FCSTD DOCUMENT  (FreeCAD 0.19R)
Label: quadcopter
License: All rights reserved
LicenseURL: http://en.wikipedia.org/wiki/All_rights_reserved
objects: Sketcher::SketchObject×3, PartDesign::Body×1
note: 4 computed .brp shape members not serialized (recipe doc carries the construction recipe); baked Part::Feature solids carry a one-line shape summary decoded from their .brp

FEATURE [Sketcher::SketchObject] Sketch001
  FullyConstrained = true
  sketch-geometry (20):
    g0: Circle CenterX=50 CenterY=-50 CenterZ=0 NormalX=0 NormalY=0 NormalZ=1 AngleXU=0 Radius=14
    g1: Circle CenterX=50 CenterY=-58 CenterZ=0 NormalX=0 NormalY=0 NormalZ=1 AngleXU=0 Radius=1.5
    g2: Circle CenterX=50 CenterY=-42 CenterZ=0 NormalX=0 NormalY=0 NormalZ=1 AngleXU=0 Radius=1.5
    g3: Circle CenterX=59.5 CenterY=-50 CenterZ=0 NormalX=0 NormalY=0 NormalZ=1 AngleXU=0 Radius=1.5
    g4: Circle CenterX=40.5 CenterY=-50 CenterZ=0 NormalX=0 NormalY=0 NormalZ=1 AngleXU=0 Radius=1.5
    g5: Circle CenterX=50 CenterY=50 CenterZ=0 NormalX=0 NormalY=0 NormalZ=1 AngleXU=0 Radius=14
    g6: Circle CenterX=50 CenterY=58 CenterZ=0 NormalX=0 NormalY=0 NormalZ=1 AngleXU=0 Radius=1.5
    g7: Circle CenterX=50 CenterY=42 CenterZ=0 NormalX=0 NormalY=0 NormalZ=1 AngleXU=0 Radius=1.5
    g8: Circle CenterX=59.5 CenterY=50 CenterZ=0 NormalX=0 NormalY=0 NormalZ=1 AngleXU=0 Radius=1.5
    g9: Circle CenterX=40.5 CenterY=50 CenterZ=0 NormalX=0 NormalY=0 NormalZ=1 AngleXU=0 Radius=1.5
    g10: Circle CenterX=-50 CenterY=-50 CenterZ=0 NormalX=0 NormalY=0 NormalZ=1 AngleXU=0 Radius=14
    g11: Circle CenterX=-50 CenterY=-58 CenterZ=0 NormalX=0 NormalY=0 NormalZ=1 AngleXU=0 Radius=1.5
    g12: Circle CenterX=-50 CenterY=-42 CenterZ=0 NormalX=0 NormalY=0 NormalZ=1 AngleXU=0 Radius=1.5
    g13: Circle CenterX=-59.5 CenterY=-50 CenterZ=0 NormalX=0 NormalY=0 NormalZ=1 AngleXU=0 Radius=1.5
    g14: Circle CenterX=-40.5 CenterY=-50 CenterZ=0 NormalX=0 NormalY=0 NormalZ=1 AngleXU=0 Radius=1.5
    g15: Circle CenterX=-50 CenterY=50 CenterZ=0 NormalX=0 NormalY=0 NormalZ=1 AngleXU=0 Radius=14
    g16: Circle CenterX=-50 CenterY=58 CenterZ=0 NormalX=0 NormalY=0 NormalZ=1 AngleXU=0 Radius=1.5
    g17: Circle CenterX=-50 CenterY=42 CenterZ=0 NormalX=0 NormalY=0 NormalZ=1 AngleXU=0 Radius=1.5
    g18: Circle CenterX=-59.5 CenterY=50 CenterZ=0 NormalX=0 NormalY=0 NormalZ=1 AngleXU=0 Radius=1.5
    g19: Circle CenterX=-40.5 CenterY=50 CenterZ=0 NormalX=0 NormalY=0 NormalZ=1 AngleXU=0 Radius=1.5
  constraints (49):
    c: Symmetric(g3,g4,g0)
    c: Symmetric(g1,g2,g0)
    c: Diameter(g0) = 28
    c: Diameter(g4) = 3
    c: Equal(g4,g1)
    c: Equal(g1,g3)
    c: Equal(g3,g2)
    c: Symmetric(g8,g9,g5)
    c: Symmetric(g6,g7,g5)
    c: Diameter(g5) = 28
    c: Diameter(g9) = 3
    c: Equal(g9,g6)
    c: Equal(g6,g8)
    c: Equal(g8,g7)
    c: Symmetric(g13,g14,g10)
    c: Symmetric(g11,g12,g10)
    c: Diameter(g10) = 28
    c: Diameter(g14) = 3
    c: Equal(g14,g11)
    c: Equal(g11,g13)
    c: Equal(g13,g12)
    c: Symmetric(g18,g19,g15)
    c: Symmetric(g16,g17,g15)
    c: DistanceX(g18,g19) = 19
    c: DistanceY(g17,g16) = 16
    c: Diameter(g15) = 28
    c: DistanceX(g15,g-1) = 50
    c: DistanceY(g-1,g15) = 50
    c: Diameter(g19) = 3
    c: Equal(g19,g16)
    c: Equal(g16,g18)
    c: Equal(g18,g17)
    c: Vertical(g16,g17)
    c: Horizontal(g18,g19)
    c: Symmetric(g10,g15,g-1)
    c: Symmetric(g0,g15,g-1)
    c: Symmetric(g5,g10,g-1)
    c: DistanceX(g13,g14) = 19
    c: DistanceY(g11,g12) = 16
    c: Horizontal(g10,g14)
    c: Vertical(g12,g10)
    c: DistanceY(g1,g2) = 16
    c: DistanceX(g4,g3) = 19
    c: Horizontal(g4,g0)
    c: Vertical(g2,g0)
    c: DistanceY(g7,g6) = 16
    c: DistanceX(g9,g8) = 19
    c: Vertical(g5,g6)
    c: Horizontal(g9,g5)
FEATURE [Sketcher::SketchObject] Sketch
  FullyConstrained = true
  MapMode = 5
  Support = -> [XY_Plane]
  sketch-geometry (4):
    g0: LineSegment StartX=-17.5 StartY=53 StartZ=0 EndX=17.5 EndY=53 EndZ=0
    g1: LineSegment StartX=17.5 StartY=53 StartZ=0 EndX=17.5 EndY=-53 EndZ=0
    g2: LineSegment StartX=17.5 StartY=-53 StartZ=0 EndX=-17.5 EndY=-53 EndZ=0
    g3: LineSegment StartX=-17.5 StartY=-53 StartZ=0 EndX=-17.5 EndY=53 EndZ=0
  constraints (11):
    c: Coincident(g0,g1)
    c: Coincident(g1,g2)
    c: Coincident(g2,g3)
    c: Coincident(g3,g0)
    c: Horizontal(g0)
    c: Horizontal(g2)
    c: Vertical(g1)
    c: Vertical(g3)
    c: DistanceY(g1,g1) = 106
    c: DistanceX(g0,g0) = 35
    c: Symmetric(g0,g1,g-1)
FEATURE [Sketcher::SketchObject] Sketch004
  FullyConstrained = true
  sketch-geometry (24):
    g0: LineSegment StartX=-7.24e-14 StartY=-3.6e-14 StartZ=0 EndX=-98.9949 EndY=-98.9949 EndZ=0
    g1: ArcOfCircle CenterX=-7.24e-14 CenterY=-3.6e-14 CenterZ=0 NormalX=0 NormalY=0 NormalZ=1 AngleXU=0 Radius=17.5 StartAngle=5.49779 EndAngle=8.63938
    g2: ArcOfCircle CenterX=-98.9949 CenterY=-98.9949 CenterZ=0 NormalX=0 NormalY=0 NormalZ=1 AngleXU=0 Radius=17.5 StartAngle=2.35619 EndAngle=5.49779
    g3: LineSegment StartX=-12.3744 StartY=12.3744 StartZ=0 EndX=-111.369 EndY=-86.6206 EndZ=0
    g4: LineSegment StartX=-86.6206 StartY=-111.369 StartZ=0 EndX=12.3744 EndY=-12.3744 EndZ=0
    g5: LineSegment StartX=-86.6206 StartY=-111.369 StartZ=0 EndX=-111.369 EndY=-86.6206 EndZ=0
    g6: LineSegment StartX=-7.24e-14 StartY=-3.6e-14 StartZ=0 EndX=98.9949 EndY=-98.9949 EndZ=0
    g7: ArcOfCircle CenterX=-7.24e-14 CenterY=-3.6e-14 CenterZ=0 NormalX=0 NormalY=0 NormalZ=1 AngleXU=0 Radius=17.5 StartAngle=0.785398 EndAngle=3.92699
    g8: ArcOfCircle CenterX=98.9949 CenterY=-98.9949 CenterZ=0 NormalX=0 NormalY=0 NormalZ=1 AngleXU=0 Radius=17.5 StartAngle=3.92699 EndAngle=7.06858
    g9: LineSegment StartX=12.3744 StartY=12.3744 StartZ=0 EndX=111.369 EndY=-86.6206 EndZ=0
    g10: LineSegment StartX=86.6206 StartY=-111.369 StartZ=0 EndX=-12.3744 EndY=-12.3744 EndZ=0
    g11: LineSegment StartX=86.6206 StartY=-111.369 StartZ=0 EndX=111.369 EndY=-86.6206 EndZ=0
    g12: LineSegment StartX=-7.24e-14 StartY=-3.6e-14 StartZ=0 EndX=-98.9949 EndY=98.9949 EndZ=0
    g13: ArcOfCircle CenterX=-7.24e-14 CenterY=-3.6e-14 CenterZ=0 NormalX=0 NormalY=0 NormalZ=1 AngleXU=0 Radius=17.5 StartAngle=3.92699 EndAngle=7.06858
    g14: ArcOfCircle CenterX=-98.9949 CenterY=98.9949 CenterZ=0 NormalX=0 NormalY=0 NormalZ=1 AngleXU=0 Radius=17.5 StartAngle=0.785398 EndAngle=3.92699
    g15: LineSegment StartX=-12.3744 StartY=-12.3744 StartZ=0 EndX=-111.369 EndY=86.6206 EndZ=0
    g16: LineSegment StartX=-86.6206 StartY=111.369 StartZ=0 EndX=12.3744 EndY=12.3744 EndZ=0
    g17: LineSegment StartX=-86.6206 StartY=111.369 StartZ=0 EndX=-111.369 EndY=86.6206 EndZ=0
    g18: LineSegment StartX=0 StartY=0 StartZ=0 EndX=98.9949 EndY=98.9949 EndZ=0
    g19: ArcOfCircle CenterX=0 CenterY=0 CenterZ=0 NormalX=0 NormalY=0 NormalZ=1 AngleXU=0 Radius=17.5 StartAngle=2.35619 EndAngle=5.49779
    g20: ArcOfCircle CenterX=98.9949 CenterY=98.9949 CenterZ=0 NormalX=0 NormalY=0 NormalZ=1 AngleXU=0 Radius=17.5 StartAngle=5.49779 EndAngle=8.63938
    g21: LineSegment StartX=12.3744 StartY=-12.3744 StartZ=0 EndX=111.369 EndY=86.6206 EndZ=0
    g22: LineSegment StartX=86.6206 StartY=111.369 StartZ=0 EndX=-12.3744 EndY=12.3744 EndZ=0
    g23: LineSegment StartX=86.6206 StartY=111.369 StartZ=0 EndX=111.369 EndY=86.6206 EndZ=0
  constraints (53):
    c: Distance(g0) = 140
    c: Tangent(g1,g3) = -1.5708
    c: Tangent(g3,g2) = -1.5708
    c: Tangent(g2,g4) = -1.5708
    c: Tangent(g4,g1) = -1.5708
    c: Equal(g1,g2)
    c: Coincident(g1,g0)
    c: Coincident(g2,g0)
    c: Coincident(g5,g2)
    c: Coincident(g5,g2)
    c: Distance(g5) = 35
    c: Distance(g6) = 140
    c: Tangent(g7,g9) = 1.5708
    c: Tangent(g9,g8) = 1.5708
    c: Tangent(g8,g10) = 1.5708
    c: Tangent(g10,g7) = 1.5708
    c: Equal(g7,g8)
    c: Coincident(g7,g6)
    c: Coincident(g8,g6)
    c: Coincident(g11,g8)
    c: Coincident(g11,g8)
    c: Distance(g11) = 35
    c: Distance(g12) = 140
    c: Tangent(g13,g15) = 1.5708
    c: Tangent(g15,g14) = 1.5708
    c: Tangent(g14,g16) = 1.5708
    c: Tangent(g16,g13) = 1.5708
    c: Equal(g13,g14)
    c: Coincident(g13,g12)
    c: Coincident(g14,g12)
    c: Coincident(g17,g14)
    c: Coincident(g17,g14)
    c: Distance(g17) = 35
    c: Coincident(g18,g-1)
    c: Angle(g-1,g18) = 0.785398
    c: Distance(g18) = 140
    c: Tangent(g19,g21) = -1.5708
    c: Tangent(g21,g20) = -1.5708
    c: Tangent(g20,g22) = -1.5708
    c: Tangent(g22,g19) = -1.5708
    c: Equal(g19,g20)
    c: Coincident(g19,g18)
    c: Coincident(g20,g18)
    c: Coincident(g23,g20)
    c: Coincident(g23,g20)
    c: Distance(g23) = 35
    c: Angle(g-2,g12) = 0.785398
    c: PointOnObject(g12,g-1)
    c: PointOnObject(g12,g-2)
    c: Angle(g0,g-1) = 2.35619
    c: Angle(g6,g-1) = 0.785398
    c: Coincident(g6,g0)
    c: Coincident(g0,g12)
FEATURE [PartDesign::Body] Body
  Group = -> [Sketch001,Sketch,Sketch004]
  Origin = -> Origin
